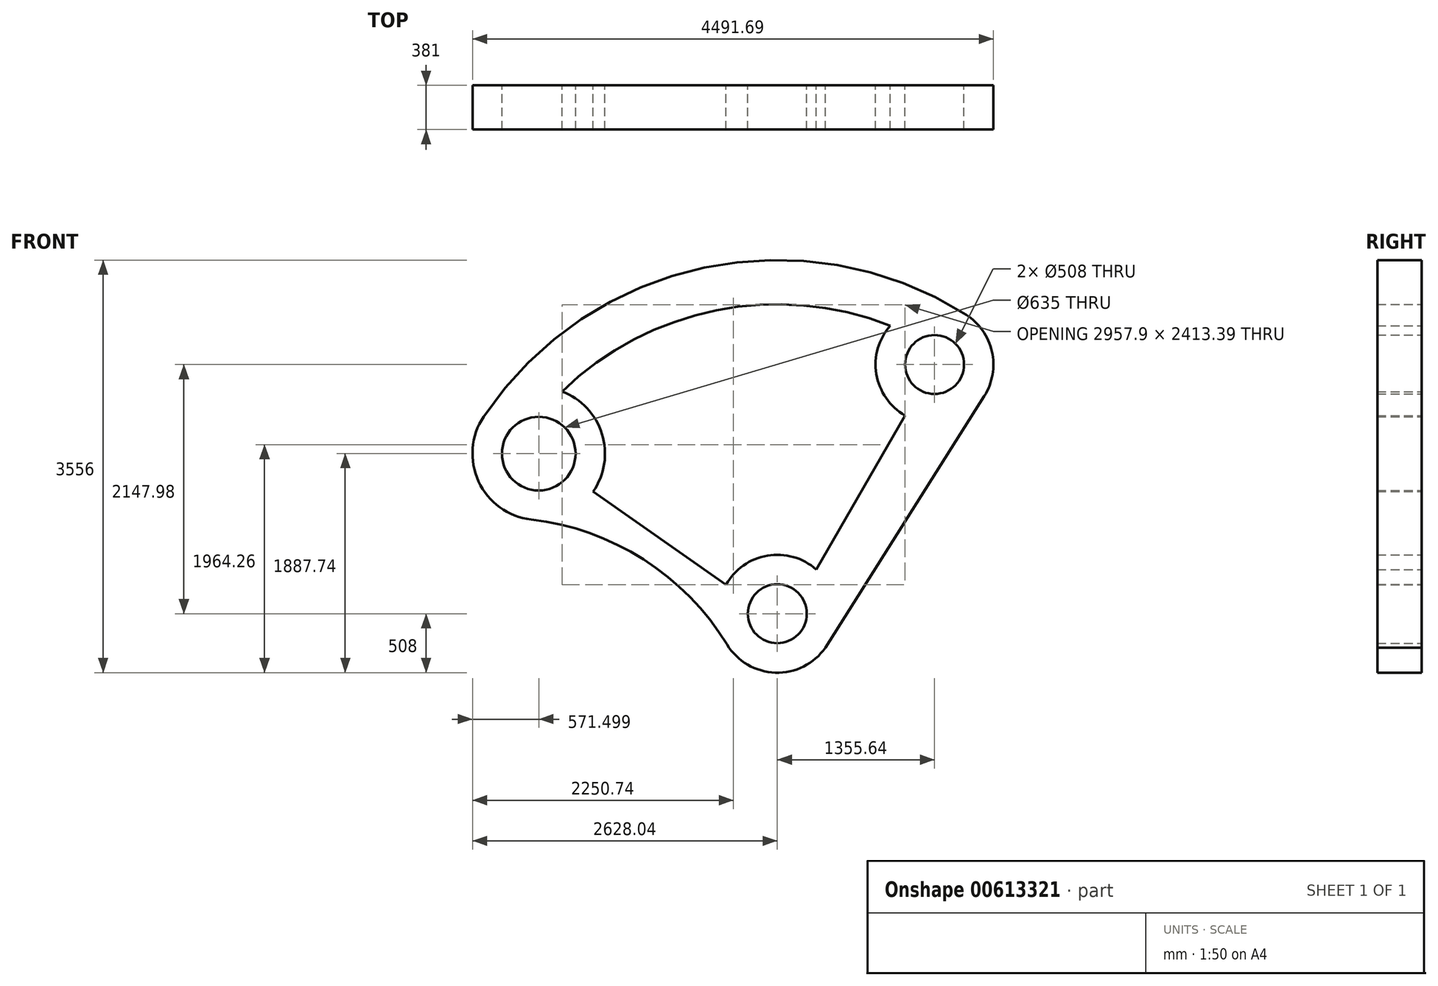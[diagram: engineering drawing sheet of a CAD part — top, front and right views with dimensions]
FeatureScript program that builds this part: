
annotation { "Feature Type Name" : "Feature", "Feature Type Description" : "" }
export const myFeature = defineFeature(function(context is Context, id is Id, definition is map)
    precondition{}
    {
        {
            var Q0;
            Q0=qCreatedBy(makeId("Front.planeOp"),FACE);
            var sketch = newSketch(context, id + "F0", { "sketchPlane" : qUnion([Q0])});
            skPoint(sketch, "E0.visualSharp", {"position": v(0, 0) * mm});
            skArc(sketch, "E1", {"start": v(1626.77, 2577.58) * mm, "mid": v(-630.72, 2982.03) * mm, "end": v(-2531.13, 1698.15) * mm});
            skCircle(sketch, "E2", {"center": v(0, 0) * mm, "radius": 254 * mm});
            skCircle(sketch, "E3", {"center": v(1355.65, 2147.98) * mm, "radius": 254 * mm});
            skArc(sketch, "E4", {"start": v(1826.98, 1942.95) * mm, "mid": v(1824.66, 1945.13) * mm, "end": v(1822.33, 1947.3) * mm});
            skCircle(sketch, "E5", {"center": v(-2056.54, 1379.74) * mm, "radius": 317.5 * mm});
            skArc(sketch, "E6", {"start": v(-1588.4, 1051.95) * mm, "mid": v(-1510.72, 1549.14) * mm, "end": v(-1856.25, 1915) * mm});
            skArc(sketch, "E7", {"start": v(-433.23, -265.29) * mm, "mid": v(9.44, -507.91) * mm, "end": v(442.78, -249.01) * mm});
            skArc(sketch, "E8", {"start": v(-433.23, -265.29) * mm, "mid": v(-1153.24, 468.12) * mm, "end": v(-2121.78, 811.98) * mm});
            skArc(sketch, "E9", {"start": v(973.69, 2482.9) * mm, "mid": v(854.43, 2065.21) * mm, "end": v(1101.65, 1708.04) * mm});
            skLineSegment(sketch, "E10", {"start": v(415.15, -292.76) * mm, "end": v(1826.98, 1942.95) * mm});
            skArc(sketch, "E11.trimOffspring", {"start": v(1785.17, 1876.74) * mm, "mid": v(1851.15, 2259.97) * mm, "end": v(1626.77, 2577.58) * mm});
            skArc(sketch, "E12.trimOffspring", {"start": v(-2531.13, 1698.15) * mm, "mid": v(-2575.36, 1140.09) * mm, "end": v(-2121.78, 811.98) * mm});
            skArc(sketch, "E13.trimOffspring", {"start": v(335.66, 381.31) * mm, "mid": v(-84.8, 500.87) * mm, "end": v(-442.47, 249.56) * mm});
            skLineSegment(sketch, "E14.trimOffspring", {"start": v(-1588.4, 1051.95) * mm, "end": v(-442.47, 249.56) * mm});
            skLineSegment(sketch, "E15.trimOffspring", {"start": v(1101.65, 1708.04) * mm, "end": v(335.66, 381.31) * mm});
            skArc(sketch, "E16.trimOffspring", {"start": v(973.69, 2482.9) * mm, "mid": v(-524.75, 2614.87) * mm, "end": v(-1856.25, 1915) * mm});
            skSolve(sketch);
        }
        {
            var Q0;
            {var subQ7=sQuery(id+"F0.wireOp",EDGE,"E1");Q0=makeQuery(id+"F0.imprint","IMPRINT",FACE,{"disambiguationData":[TD([[makeQuery(id+"F0.imprint","IMPRINT",EDGE,{"derivedFrom":subQ7}),1.0]])]});}
            extrude(context, id + "F1", {"entities" : qUnion([Q0]), "depth" : 381 * mm, "offsetDistance" : 25.4 * mm});
        }
    });
